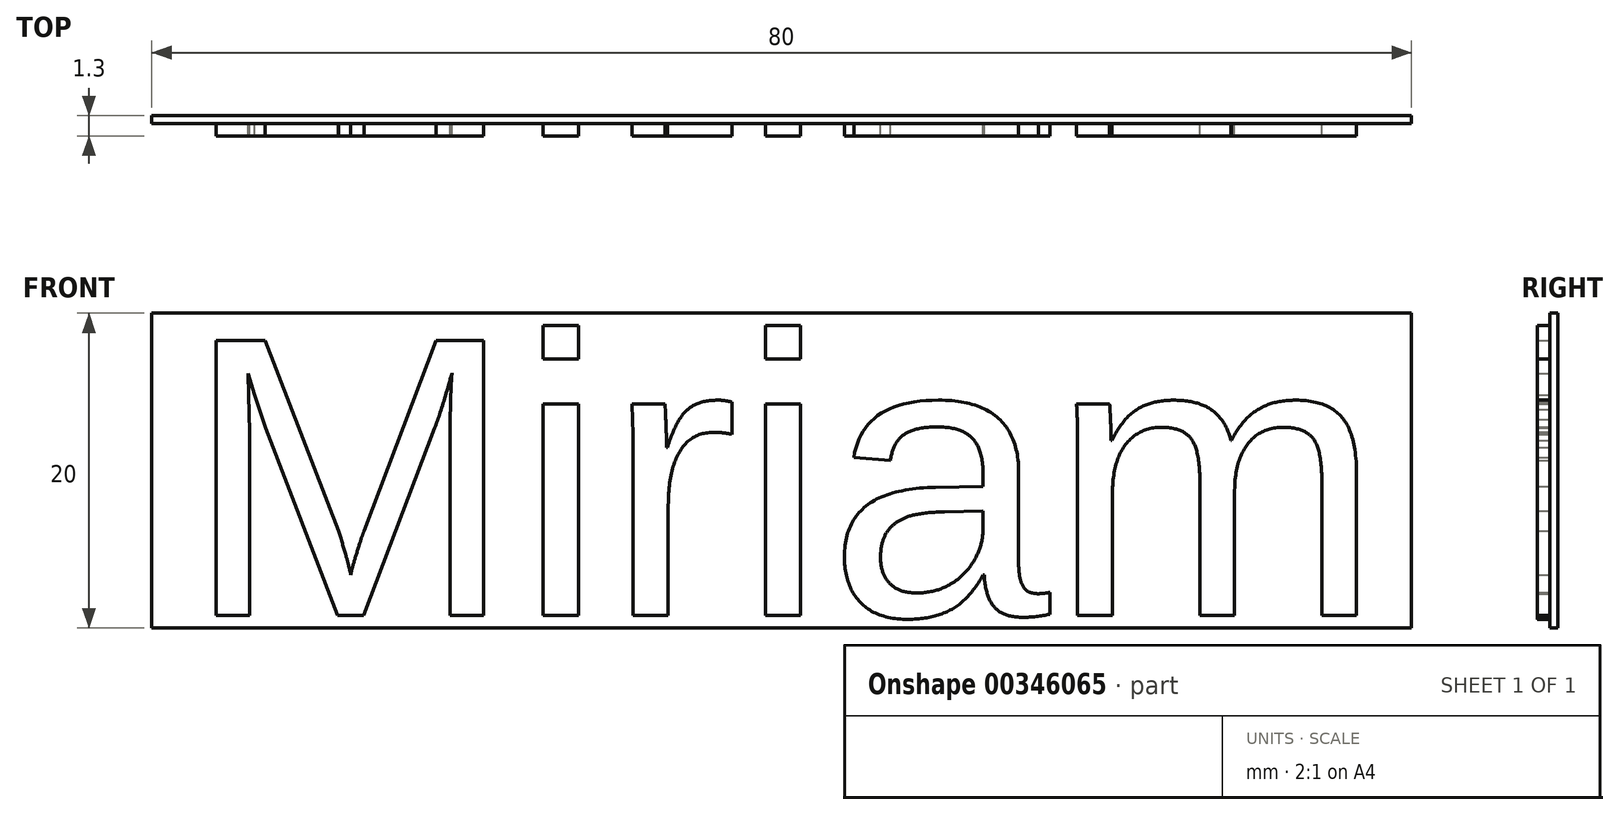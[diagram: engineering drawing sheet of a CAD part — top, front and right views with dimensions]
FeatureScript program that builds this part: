
annotation { "Feature Type Name" : "Feature", "Feature Type Description" : "" }
export const myFeature = defineFeature(function(context is Context, id is Id, definition is map)
    precondition{}
    {
        {
            var Q0;
            Q0=qCreatedBy(makeId("Front.planeOp"),FACE);
            var sketch = newSketch(context, id + "F0", { "sketchPlane" : qUnion([Q0])});
            skLineSegment(sketch, "E0.bottom", {"start": v(40, -10) * mm, "end": v(-40, -10) * mm});
            skLineSegment(sketch, "E0.top", {"start": v(40, 10) * mm, "end": v(-40, 10) * mm});
            skLineSegment(sketch, "E0.left", {"start": v(40, -10) * mm, "end": v(40, 10) * mm});
            skLineSegment(sketch, "E0.right", {"start": v(-40, -10) * mm, "end": v(-40, 10) * mm});
            skPoint(sketch, "E0.middle", {"position": v(0, 0) * mm});
            skSolve(sketch);
        }
        {
            var Q0;
            Q0=makeQuery(id+"F0.imprint","IMPRINT",FACE,{"disambiguationData":[TD([[makeQuery(id+"F0.imprint","IMPRINT",EDGE,{"derivedFrom":sQuery(id+"F0.wireOp",EDGE,"E0.bottom")}),-1.0]])]});
            extrude(context, id + "F1", {"entities" : qUnion([Q0]), "oppositeDirection" : true, "depth" : 0.5 * mm});
        }
        {
            var Q0;
            Q0=makeQuery(id+"F1.opExtrude","CAP_FACE",FACE,{"disambiguationData":[OSD([sQuery(id+"F0.wireOp",EDGE,"E0.bottom"),sQuery(id+"F0.wireOp",EDGE,"E0.top"),sQuery(id+"F0.wireOp",EDGE,"E0.left"),sQuery(id+"F0.wireOp",EDGE,"E0.right")])],"isStart":true});
            var sketch = newSketch(context, id + "F2", { "sketchPlane" : qUnion([Q0])});
            skText(sketch, "E1", { "text": "Miriam", "fontName": "Arimo-Regular.ttf"});
            const initialGuessF2  = {"E1": [-0.038, -0.0092, 1, 0, 0.01829]};
            skSetInitialGuess(sketch, initialGuessF2);
            skSolve(sketch);
        }
        {
            var Q0;
            Q0 = qSketchRegion(id + "F2", true);
            extrude(context, id + "F3", {"entities" : qUnion([Q0]), "operationType" : NewBodyOperationType.ADD, "depth" : 0.8 * mm});
        }
    });
